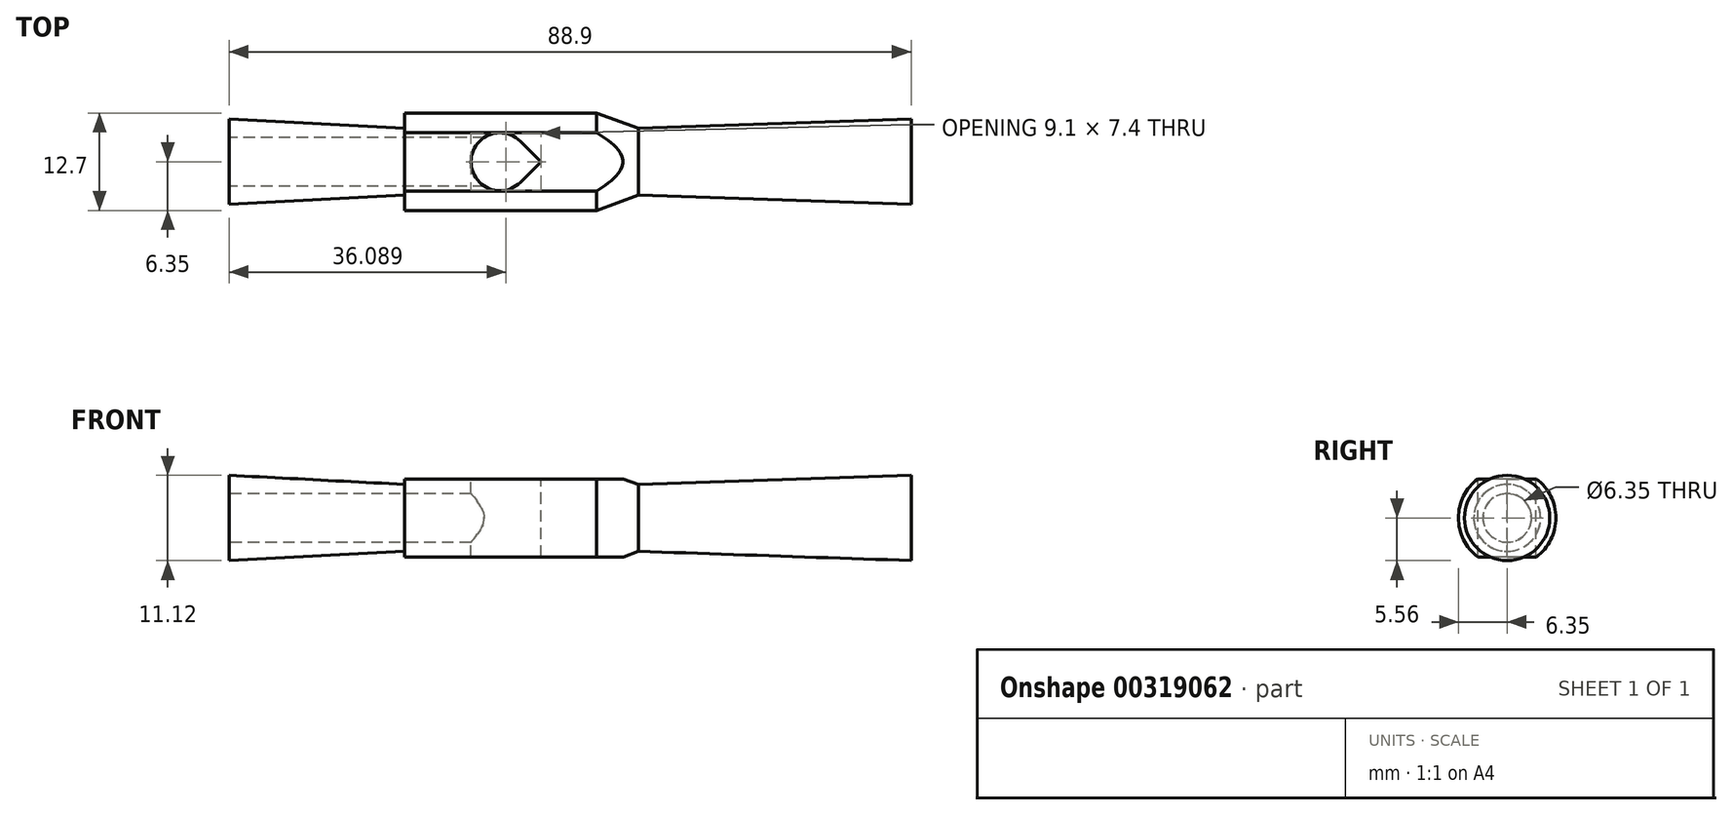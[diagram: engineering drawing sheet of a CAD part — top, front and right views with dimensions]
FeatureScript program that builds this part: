
annotation { "Feature Type Name" : "Feature", "Feature Type Description" : "" }
export const myFeature = defineFeature(function(context is Context, id is Id, definition is map)
    precondition{}
    {
        {
            var Q0;
            Q0=qCreatedBy(makeId("Front.planeOp"),FACE);
            var sketch = newSketch(context, id + "F0", { "sketchPlane" : qUnion([Q0])});
            skLineSegment(sketch, "E0", {"start": v(-38.1, 0) * mm, "end": v(0, 0) * mm});
            skLineSegment(sketch, "E1", {"start": v(0, 0) * mm, "end": v(50.8, 0) * mm});
            skLineSegment(sketch, "E2", {"start": v(50.8, 0) * mm, "end": v(50.8, 5.56) * mm});
            skLineSegment(sketch, "E3", {"start": v(50.8, 5.56) * mm, "end": v(15.24, 4.36) * mm});
            skLineSegment(sketch, "E4", {"start": v(15.24, 4.36) * mm, "end": v(15.24, 6.35) * mm});
            skLineSegment(sketch, "E5", {"start": v(15.24, 6.35) * mm, "end": v(-15.24, 6.35) * mm});
            skLineSegment(sketch, "E6", {"start": v(-15.24, 6.35) * mm, "end": v(-15.24, 4.36) * mm});
            skLineSegment(sketch, "E7", {"start": v(-15.24, 4.36) * mm, "end": v(-38.1, 5.56) * mm});
            skLineSegment(sketch, "E8", {"start": v(-38.1, 5.56) * mm, "end": v(-38.1, 0) * mm});
            skSolve(sketch);
        }
        {
            var Q0;
            Q0=makeQuery(id+"F0.imprint","IMPRINT",FACE,{"disambiguationData":[TD([[makeQuery(id+"F0.imprint","IMPRINT",EDGE,{"derivedFrom":sQuery(id+"F0.wireOp",EDGE,"E0")}),1.0]])]});
            var Q1;
            Q1=sQuery(id+"F0.wireOp",EDGE,"E0");
            revolve(context, id + "F1", {"entities" : qUnion([Q0]), "axis" : qUnion([Q1]), "revolveType" : RevolveType.FULL});
        }
        {
            var Q0;
            Q0=qCreatedBy(makeId("Front.planeOp"),FACE);
            var sketch = newSketch(context, id + "F2", { "sketchPlane" : qUnion([Q0])});
            skLineSegment(sketch, "E9.0", {"start": v(15.24, -4.36) * mm, "end": v(15.24, 4.36) * mm, "construction": true});
            skLineSegment(sketch, "E10", {"start": v(15.24, 4.36) * mm, "end": v(9.77, 6.35) * mm});
            skLineSegment(sketch, "E11", {"start": v(15.24, 6.35) * mm, "end": v(6.04, 6.35) * mm});
            skLineSegment(sketch, "E12", {"start": v(15.24, 6.35) * mm, "end": v(15.24, 4.36) * mm});
            skLineSegment(sketch, "E13", {"start": v(11.05, 0) * mm, "end": v(20.38, 0) * mm, "construction": true});
            skSolve(sketch);
        }
        {
            var Q0;
            Q0 = qSketchRegion(id + "F2", true);
            var Q1;
            Q1=sQuery(id+"F2.wireOp",EDGE,"E13");
            revolve(context, id + "F3", {"operationType" : NewBodyOperationType.REMOVE, "entities" : qUnion([Q0]), "axis" : qUnion([Q1]), "revolveType" : RevolveType.FULL, "oppositeDirection" : true});
        }
        {
            var Q0;
            Q0=qCreatedBy(makeId("Front.planeOp"),FACE);
            var sketch = newSketch(context, id + "F4", { "sketchPlane" : qUnion([Q0])});
            skLineSegment(sketch, "E14.bottom", {"start": v(-15.86, 16.96) * mm, "end": v(17.44, 16.96) * mm});
            skLineSegment(sketch, "E14.top", {"start": v(-15.86, 5.08) * mm, "end": v(17.44, 5.08) * mm});
            skLineSegment(sketch, "E14.left", {"start": v(-15.86, 16.96) * mm, "end": v(-15.86, 5.08) * mm});
            skLineSegment(sketch, "E14.right", {"start": v(17.44, 16.96) * mm, "end": v(17.44, 5.08) * mm});
            skLineSegment(sketch, "E15.bottom", {"start": v(-19.27, -15.32) * mm, "end": v(19.2, -15.32) * mm});
            skLineSegment(sketch, "E15.top", {"start": v(-19.27, -5.08) * mm, "end": v(19.2, -5.08) * mm});
            skLineSegment(sketch, "E15.left", {"start": v(-19.27, -15.32) * mm, "end": v(-19.27, -5.08) * mm});
            skLineSegment(sketch, "E15.right", {"start": v(19.2, -15.32) * mm, "end": v(19.2, -5.08) * mm});
            skLineSegment(sketch, "E16", {"start": v(-12.07, 0) * mm, "end": v(13.33, 0) * mm, "construction": true});
            skSolve(sketch);
        }
        {
            var Q0;
            Q0 = qSketchRegion(id + "F4", true);
            extrude(context, id + "F5", {"entities" : qUnion([Q0]), "operationType" : NewBodyOperationType.REMOVE, "endBound" : BoundingType.SYMMETRIC, "depth" : 25.4 * mm});
        }
        {
            var Q0;
            Q0=makeQuery(id+"F5.boolean.opBoolean","COPY",FACE,{"derivedFrom":makeQuery(id+"F5.opExtrude","SWEPT_FACE",FACE,{"disambiguationData":[OSD([sQuery(id+"F4.wireOp",EDGE,"E14.top")])]})});
            var sketch = newSketch(context, id + "F6", { "sketchPlane" : qUnion([Q0])});
            skArc(sketch, "E17", {"start": v(-0.13, 2.67) * mm, "mid": v(-6.56, 0) * mm, "end": v(-0.13, -2.67) * mm});
            skLineSegment(sketch, "E18", {"start": v(2.54, 0) * mm, "end": v(-0.13, 2.67) * mm});
            skLineSegment(sketch, "E19", {"start": v(2.54, 0) * mm, "end": v(-0.13, -2.67) * mm});
            skLineSegment(sketch, "E20", {"start": v(2.54, 0) * mm, "end": v(-2.8, 0) * mm, "construction": true});
            skPoint(sketch, "E21", {"position": v(-2.8, 3.77) * mm});
            skPoint(sketch, "E22", {"position": v(-2.8, -3.77) * mm});
            skPoint(sketch, "E23.orphan", {"position": v(-1.23, 3.77) * mm});
            skPoint(sketch, "E24.orphan", {"position": v(-1.23, -3.77) * mm});
            skPoint(sketch, "E25", {"position": v(-6.56, 0) * mm});
            skSolve(sketch);
        }
        {
            var Q0;
            Q0 = qSketchRegion(id + "F6", true);
            extrude(context, id + "F7", {"entities" : qUnion([Q0]), "operationType" : NewBodyOperationType.REMOVE, "endBound" : BoundingType.THROUGH_ALL, "oppositeDirection" : true, "depth" : 25.4 * mm});
        }
        {
            var Q0;
            Q0=makeQuery(id+"F1.opRevolve","SWEPT_FACE",FACE,{"disambiguationData":[OSD([sQuery(id+"F0.wireOp",EDGE,"E8")])]});
            var sketch = newSketch(context, id + "F8", { "sketchPlane" : qUnion([Q0])});
            skCircle(sketch, "E26", {"center": v(0, 0) * mm, "radius": 3.18 * mm});
            skSolve(sketch);
        }
        {
            var Q0;
            Q0 = qSketchRegion(id + "F8", true);
            extrude(context, id + "F9", {"entities" : qUnion([Q0]), "operationType" : NewBodyOperationType.REMOVE, "endBound" : BoundingType.UP_TO_NEXT, "oppositeDirection" : true, "depth" : 25.4 * mm});
        }
    });
